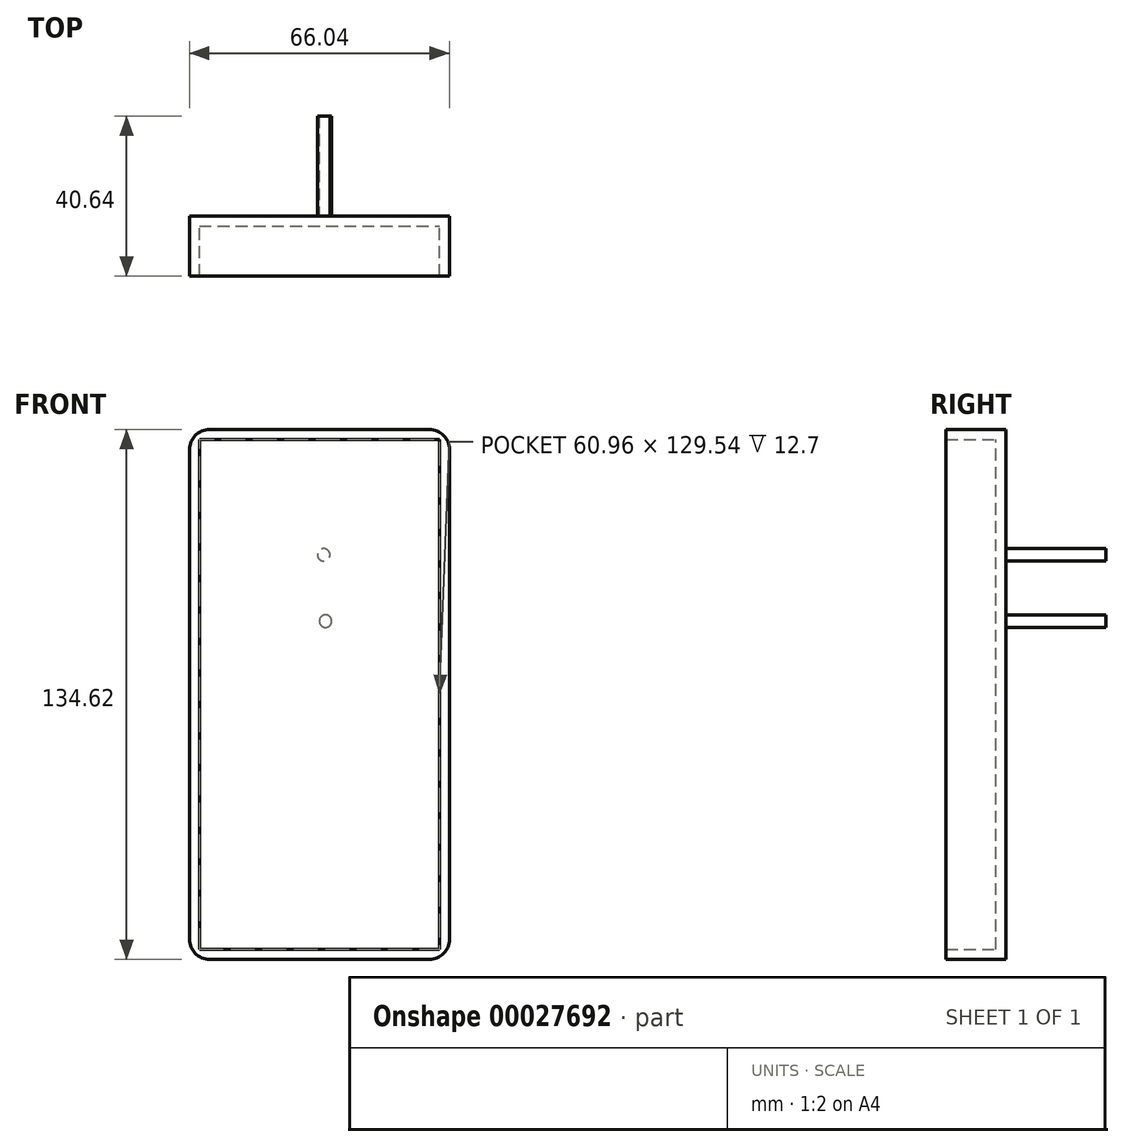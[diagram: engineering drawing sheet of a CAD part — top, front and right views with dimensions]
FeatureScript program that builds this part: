
annotation { "Feature Type Name" : "Feature", "Feature Type Description" : "" }
export const myFeature = defineFeature(function(context is Context, id is Id, definition is map)
    precondition{}
    {
        {
            var Q0;
            Q0=qCreatedBy(makeId("Front.planeOp"),FACE);
            var sketch = newSketch(context, id + "F0", { "sketchPlane" : qUnion([Q0])});
            skLineSegment(sketch, "E0.bottom", {"start": v(-43.1, -35.89) * mm, "end": v(22.93, -35.89) * mm});
            skLineSegment(sketch, "E0.top", {"start": v(-43.1, 98.73) * mm, "end": v(22.93, 98.73) * mm});
            skLineSegment(sketch, "E0.left", {"start": v(-43.1, -35.89) * mm, "end": v(-43.1, 98.73) * mm});
            skLineSegment(sketch, "E0.right", {"start": v(22.93, -35.89) * mm, "end": v(22.93, 98.73) * mm});
            skSolve(sketch);
        }
        {
            var Q0;
            Q0 = qSketchRegion(id + "F0", true);
            extrude(context, id + "F1", {"entities" : qUnion([Q0]), "depth" : 15.24 * mm});
        }
        {
            var Q0;
            Q0=makeQuery(id+"F1.opExtrude","CAP_FACE",FACE,{"disambiguationData":[OSD([sQuery(id+"F0.wireOp",EDGE,"E0.bottom"),sQuery(id+"F0.wireOp",EDGE,"E0.top"),sQuery(id+"F0.wireOp",EDGE,"E0.left"),sQuery(id+"F0.wireOp",EDGE,"E0.right")])],"isStart":false});
            shell(context, id + "F2", {"entities" : qUnion([Q0]), "thickness" : 2.54 * mm});
        }
        {
            var Q0;
            Q0=makeQuery(id+"F1.opExtrude","SWEPT_EDGE",EDGE,{"disambiguationData":[OSD([sQuery(id+"F0.wireOp",EDGE,"E0.top"),sQuery(id+"F0.wireOp",EDGE,"E0.left")])]});
            var Q1;
            Q1=makeQuery(id+"F1.opExtrude","SWEPT_EDGE",EDGE,{"disambiguationData":[OSD([sQuery(id+"F0.wireOp",EDGE,"E0.top"),sQuery(id+"F0.wireOp",EDGE,"E0.right")])]});
            var Q2;
            Q2=makeQuery(id+"F1.opExtrude","SWEPT_EDGE",EDGE,{"disambiguationData":[OSD([sQuery(id+"F0.wireOp",EDGE,"E0.bottom"),sQuery(id+"F0.wireOp",EDGE,"E0.right")])]});
            var Q3;
            Q3=makeQuery(id+"F1.opExtrude","SWEPT_EDGE",EDGE,{"disambiguationData":[OSD([sQuery(id+"F0.wireOp",EDGE,"E0.bottom"),sQuery(id+"F0.wireOp",EDGE,"E0.left")])]});
            fillet(context, id + "F3", {"entities" : qUnion([Q0, Q1, Q2, Q3]), "radius" : 5.08 * mm, "tangentPropagation" : true, "allowEdgeOverflow" : false});
        }
        {
            var Q0;
            Q0=makeQuery(id+"F2.opShell","OFFSET_FACE",FACE,{"disambiguationData":[OSD([sQuery(id+"F0.wireOp",EDGE,"E0.bottom"),sQuery(id+"F0.wireOp",EDGE,"E0.top"),sQuery(id+"F0.wireOp",EDGE,"E0.left"),sQuery(id+"F0.wireOp",EDGE,"E0.right")])]});
            var sketch = newSketch(context, id + "F4", { "sketchPlane" : qUnion([Q0])});
            skLineSegment(sketch, "E1.bottom", {"start": v(-40.57, 96.2) * mm, "end": v(20.4, 96.2) * mm});
            skLineSegment(sketch, "E1.top", {"start": v(-40.57, -33.35) * mm, "end": v(20.4, -33.35) * mm});
            skLineSegment(sketch, "E1.left", {"start": v(-40.57, 96.2) * mm, "end": v(-40.57, -33.35) * mm});
            skLineSegment(sketch, "E1.right", {"start": v(20.4, 96.2) * mm, "end": v(20.4, -33.35) * mm});
            skSolve(sketch);
        }
        {
            var Q0;
            Q0=makeQuery(id+"F1.opExtrude","CAP_FACE",FACE,{"disambiguationData":[OSD([sQuery(id+"F0.wireOp",EDGE,"E0.bottom"),sQuery(id+"F0.wireOp",EDGE,"E0.top"),sQuery(id+"F0.wireOp",EDGE,"E0.left"),sQuery(id+"F0.wireOp",EDGE,"E0.right")])],"isStart":true});
            var sketch = newSketch(context, id + "F5", { "sketchPlane" : qUnion([Q0])});
            skCircle(sketch, "E2", {"center": v(9, 66.91) * mm, "radius": 1.59 * mm});
            skSolve(sketch);
        }
        {
            var Q0;
            Q0 = qSketchRegion(id + "F5", true);
            extrude(context, id + "F6", {"entities" : qUnion([Q0]), "operationType" : NewBodyOperationType.ADD, "depth" : 25.4 * mm});
        }
        {
            var Q0;
            Q0 = qSketchRegion(id + "F5", true);
            extrude(context, id + "F7", {"entities" : qUnion([Q0]), "operationType" : NewBodyOperationType.ADD, "depth" : 25.4 * mm});
        }
        {
            var Q0;
            Q0=makeQuery(id+"F1.opExtrude","CAP_FACE",FACE,{"disambiguationData":[OSD([sQuery(id+"F0.wireOp",EDGE,"E0.bottom"),sQuery(id+"F0.wireOp",EDGE,"E0.top"),sQuery(id+"F0.wireOp",EDGE,"E0.left"),sQuery(id+"F0.wireOp",EDGE,"E0.right")])],"isStart":true});
            var sketch = newSketch(context, id + "F8", { "sketchPlane" : qUnion([Q0])});
            skCircle(sketch, "E3", {"center": v(8.54, 50.05) * mm, "radius": 1.59 * mm});
            skSolve(sketch);
        }
        {
            var Q0;
            Q0 = qSketchRegion(id + "F8", true);
            extrude(context, id + "F9", {"entities" : qUnion([Q0]), "operationType" : NewBodyOperationType.ADD, "depth" : 25.4 * mm});
        }
    });
